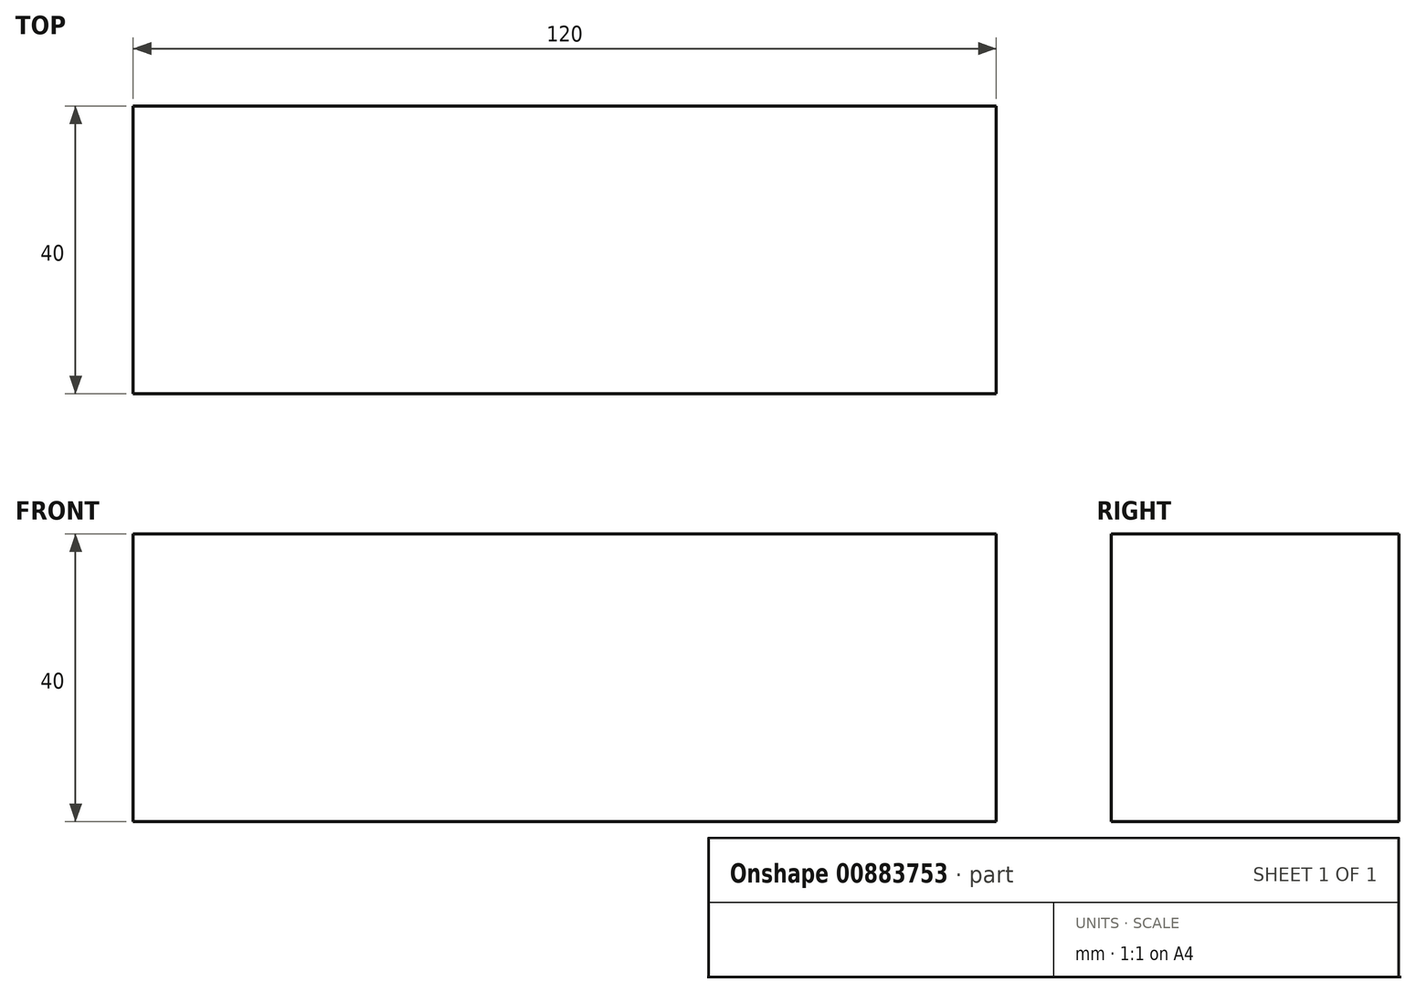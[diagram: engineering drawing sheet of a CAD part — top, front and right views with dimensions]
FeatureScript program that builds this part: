
annotation { "Feature Type Name" : "Feature", "Feature Type Description" : "" }
export const myFeature = defineFeature(function(context is Context, id is Id, definition is map)
    precondition{}
    {
        {
            var Q0;
            Q0=qCreatedBy(makeId("Right.planeOp"),FACE);
            var sketch = newSketch(context, id + "F0", { "sketchPlane" : qUnion([Q0])});
            skLineSegment(sketch, "E0.bottom", {"start": v(114.97, 25.32) * mm, "end": v(74.97, 25.32) * mm});
            skLineSegment(sketch, "E0.top", {"start": v(114.97, 65.32) * mm, "end": v(74.97, 65.32) * mm});
            skLineSegment(sketch, "E0.left", {"start": v(114.97, 25.32) * mm, "end": v(114.97, 65.32) * mm});
            skLineSegment(sketch, "E0.right", {"start": v(74.97, 25.32) * mm, "end": v(74.97, 65.32) * mm});
            skPoint(sketch, "E0.middle", {"position": v(94.97, 45.32) * mm});
            skSolve(sketch);
        }
        {
            var Q0;
            Q0 = qSketchRegion(id + "F0", true);
            extrude(context, id + "F1", {"entities" : qUnion([Q0]), "depth" : 120 * mm, "offsetDistance" : 25 * mm});
        }
    });
